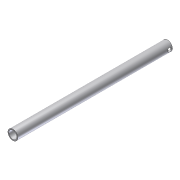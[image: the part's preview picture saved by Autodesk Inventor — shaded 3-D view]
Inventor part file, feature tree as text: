
AUTODESK INVENTOR PART (.ipt)
format: ipt  version: unknown  size: 167,424 bytes
history: native  units: in
note: dims shown in document units (in); Inventor stores cm internally (conversion verified against a paired STEP export)
features: extrude x2, sketch x2, shell x1, plane x1
ambient origin geometry x8: Origin, YZ Plane, XZ Plane, XY Plane, X Axis, Y Axis, Z Axis, Center Point
feature tree (6):
  extrude  "Extrusion1"  Depth=20.5in TaperAngle=0.0deg
  shell  "Shell1"  Thickness=0.133in
  plane  "Work Plane1"
  extrude  "Extrusion2"  Depth=0.375in
  sketch  "Sketch1"  dims[d0=1.315in d1=20.5in d2=0.0in d3=0.133in]
  sketch  "Sketch3"  dims[d4=0.5in d5=0.375in d6=1.0in d7=0.0in]
